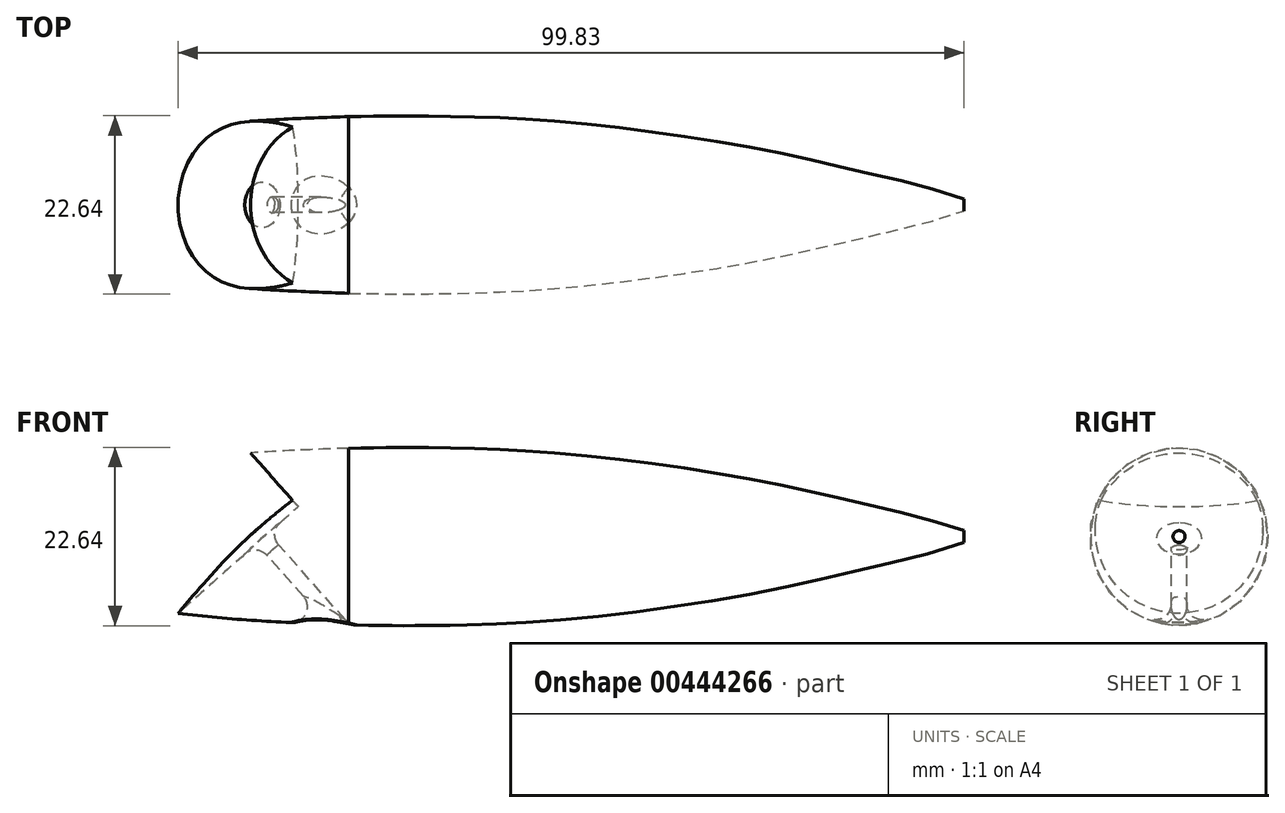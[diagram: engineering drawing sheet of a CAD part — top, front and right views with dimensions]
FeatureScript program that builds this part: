
annotation { "Feature Type Name" : "Feature", "Feature Type Description" : "" }
export const myFeature = defineFeature(function(context is Context, id is Id, definition is map)
    precondition{}
    {
        {
            var Q0;
            Q0=qCreatedBy(makeId("Top.planeOp"),FACE);
            var sketch = newSketch(context, id + "F0", { "sketchPlane" : qUnion([Q0])});
            skFitSpline(sketch, "E0", {"points": [v(50.74, 0.76) * mm, v(40.36, 3.6) * mm, v(27.98, 6.45) * mm, v(13.03, 9.02) * mm, v(-1.08, 10.63) * mm, v(-11.73, 11.19) * mm, v(-22.12, 11.3) * mm, v(-27.42, 11.23) * mm], "startDerivative": vector(-105.08, 35.47) * mm, "endDerivative": vector(-52.2, -0.15) * mm});
            skLineSegment(sketch, "E1", {"start": v(0, 0) * mm, "end": v(-76.2, 0) * mm});
            skFitSpline(sketch, "E2.MirrorCS", {"points": [v(50.74, -0.76) * mm, v(40.36, -3.6) * mm, v(27.98, -6.45) * mm, v(13.03, -9.02) * mm, v(-1.08, -10.63) * mm, v(-11.73, -11.19) * mm, v(-22.12, -11.3) * mm, v(-27.42, -11.23) * mm], "startDerivative": vector(-105.08, -35.47) * mm, "endDerivative": vector(-52.2, 0.15) * mm});
            skLineSegment(sketch, "E3", {"start": v(50.74, 0.76) * mm, "end": v(50.74, -0.76) * mm});
            skLineSegment(sketch, "E4", {"start": v(-27.42, 11.23) * mm, "end": v(-27.42, -11.23) * mm});
            skFitSpline(sketch, "E5", {"points": [v(-27.42, -11.23) * mm, v(-50.83, -9.56) * mm], "startDerivative": vector(-27.1, 0.96) * mm, "endDerivative": vector(-25.61, 3.15) * mm});
            skLineSegment(sketch, "E6", {"start": v(-27.42, 0) * mm, "end": v(50.74, 0) * mm});
            skFitSpline(sketch, "E7.MirrorCS", {"points": [v(-27.42, 11.23) * mm, v(-50.83, 9.56) * mm], "startDerivative": vector(-27.1, -0.96) * mm, "endDerivative": vector(-25.61, -3.15) * mm});
            skLineSegment(sketch, "E8", {"start": v(-50.83, -9.56) * mm, "end": v(-50.83, 9.56) * mm});
            skSolve(sketch);
        }
        {
            var Q0;
            {var subQ5=sQuery(id+"F0.wireOp",EDGE,"E0");Q0=makeQuery(id+"F0.imprint","IMPRINT",FACE,{"disambiguationData":[TD([[makeQuery(id+"F0.imprint","IMPRINT",EDGE,{"derivedFrom":subQ5}),1.0]])]});}
            var Q1;
            {var subQ5=sQuery(id+"F0.wireOp",EDGE,"E7.MirrorCS");Q1=makeQuery(id+"F0.imprint","IMPRINT",FACE,{"disambiguationData":[TD([[makeQuery(id+"F0.imprint","IMPRINT",EDGE,{"derivedFrom":subQ5}),1.0]])]});}
            var Q2;
            Q2=sQuery(id+"F0.wireOp",EDGE,"E1");
            revolve(context, id + "F1", {"entities" : qUnion([Q0, Q1]), "axis" : qUnion([Q2]), "revolveType" : RevolveType.FULL});
        }
        {
            var Q0;
            Q0=qCreatedBy(makeId("Front.planeOp"),FACE);
            var sketch = newSketch(context, id + "F2", { "sketchPlane" : qUnion([Q0])});
            skLineSegment(sketch, "E9.0", {"start": v(-50.83, 9.56) * mm, "end": v(-50.83, -9.56) * mm});
            skLineSegment(sketch, "E10", {"start": v(-50.83, -9.56) * mm, "end": v(-34.7, 4.79) * mm});
            skLineSegment(sketch, "E11", {"start": v(-34.7, 4.79) * mm, "end": v(-39.93, 10.67) * mm});
            skFitSpline(sketch, "E12", {"points": [v(-39.93, 10.67) * mm, v(-50.83, 9.56) * mm], "startDerivative": vector(-10.94, -0.63) * mm, "endDerivative": vector(-11.09, -1.8) * mm});
            skSolve(sketch);
        }
        {
            var Q0;
            Q0=makeQuery(id+"F2.imprint","IMPRINT",FACE,{"disambiguationData":[TD([[makeQuery(id+"F2.imprint","IMPRINT",EDGE,{"derivedFrom":sQuery(id+"F2.wireOp",EDGE,"E9.0")}),1.0]])]});
            extrude(context, id + "F3", {"entities" : qUnion([Q0]), "operationType" : NewBodyOperationType.REMOVE, "endBound" : BoundingType.SYMMETRIC, "oppositeDirection" : true, "depth" : 25.4 * mm});
        }
        {
            var Q0;
            Q0=makeQuery(id+"F3.boolean.opBoolean","COPY",FACE,{"derivedFrom":makeQuery(id+"F3.opExtrude","SWEPT_FACE",FACE,{"disambiguationData":[OSD([sQuery(id+"F2.wireOp",EDGE,"E11")])]})});
            var sketch = newSketch(context, id + "F4", { "sketchPlane" : qUnion([Q0])});
            skFitSpline(sketch, "E13", {"points": [v(10.62, 26.64) * mm, v(-10.64, 26.64) * mm], "startDerivative": vector(-14.87, -5.24) * mm, "endDerivative": vector(-14.04, 5.24) * mm});
            skLineSegment(sketch, "E14", {"start": v(-10.64, 26.64) * mm, "end": v(10.62, 26.64) * mm});
            skSolve(sketch);
        }
        {
            var Q0;
            {var subQ0=sQuery(id+"F4.wireOp",EDGE,"E13");Q0=makeQuery(id+"F4.imprint","IMPRINT",FACE,{"disambiguationData":[TD([[makeQuery(id+"F4.imprint","IMPRINT",EDGE,{"derivedFrom":subQ0}),-1.0]])]});}
            extrude(context, id + "F5", {"entities" : qUnion([Q0]), "operationType" : NewBodyOperationType.REMOVE, "endBound" : BoundingType.THROUGH_ALL, "depth" : 25.4 * mm});
        }
        {
            var Q0;
            Q0=makeQuery(id+"F3.boolean.opBoolean","COPY",FACE,{"derivedFrom":makeQuery(id+"F3.opExtrude","SWEPT_FACE",FACE,{"disambiguationData":[OSD([sQuery(id+"F2.wireOp",EDGE,"E10")])]})});
            var sketch = newSketch(context, id + "F6", { "sketchPlane" : qUnion([Q0])});
            skLineSegment(sketch, "E15", {"start": v(-21.97, 0) * mm, "end": v(-28.83, 0) * mm, "construction": true});
            skCircle(sketch, "E16", {"center": v(-28.83, 0) * mm, "radius": 1 * mm});
            skSolve(sketch);
        }
        {
            var Q0;
            Q0=makeQuery(id+"F6.imprint","IMPRINT",FACE,{"disambiguationData":[TD([[makeQuery(id+"F6.imprint","IMPRINT",EDGE,{"derivedFrom":sQuery(id+"F6.wireOp",EDGE,"E16")}),1.0]])]});
            extrude(context, id + "F7", {"entities" : qUnion([Q0]), "operationType" : NewBodyOperationType.REMOVE, "oppositeDirection" : true, "depth" : 25.4 * mm});
        }
        {
            var Q0;
            Q0=makeQuery(id+"F7.boolean.opBoolean","INTERSECT",EDGE,{"derivedFrom":[makeQuery(id+"F5.boolean.opBoolean","COPY",FACE,{"derivedFrom":makeQuery(id+"F5.opExtrude","SWEPT_FACE",FACE,{"disambiguationData":[OSD([sQuery(id+"F4.wireOp",EDGE,"E13")])]})}),makeQuery(id+"F7.opExtrude","SWEPT_FACE",FACE,{"disambiguationData":[OSD([sQuery(id+"F6.wireOp",EDGE,"E16")])]})]});
            fillet(context, id + "F8", {"entities" : qUnion([Q0]), "radius" : 2 * mm, "tangentPropagation" : true, "allowEdgeOverflow" : false});
        }
        {
            var Q0;
            Q0=makeQuery(id+"F7.boolean.opBoolean","INTERSECT",EDGE,{"derivedFrom":[makeQuery(id+"F1.opRevolve","SWEPT_FACE",FACE,{"disambiguationData":[OSD([sQuery(id+"F0.wireOp",EDGE,"E7.MirrorCS")])]}),makeQuery(id+"F7.opExtrude","SWEPT_FACE",FACE,{"disambiguationData":[OSD([sQuery(id+"F6.wireOp",EDGE,"E16")])]})]});
            var Q1;
            Q1=makeQuery(id+"F7.boolean.opBoolean","INTERSECT",EDGE,{"derivedFrom":[makeQuery(id+"F1.opRevolve","SWEPT_FACE",FACE,{"disambiguationData":[OSD([sQuery(id+"F0.wireOp",EDGE,"E0")])]}),makeQuery(id+"F7.opExtrude","SWEPT_FACE",FACE,{"disambiguationData":[OSD([sQuery(id+"F6.wireOp",EDGE,"E16")])]})]});
            fillet(context, id + "F9", {"entities" : qUnion([Q0, Q1]), "radius" : 2 * mm, "tangentPropagation" : true, "allowEdgeOverflow" : false});
        }
        {
            var Q0;
            Q0=qCreatedBy(makeId("Front.planeOp"),FACE);
            var sketch = newSketch(context, id + "F10", { "sketchPlane" : qUnion([Q0])});
            skFitSpline(sketch, "E17.0", {"points": [v(-34.7, 4.79) * mm, v(-34.12, 4.14) * mm, v(-33.83, 3.82) * mm, v(-33.83, 3.81) * mm]});
            skPoint(sketch, "E18", {"position": v(-34.55, 4.62) * mm});
            skLineSegment(sketch, "E19", {"start": v(-34.55, 4.62) * mm, "end": v(50.9, 0) * mm});
            skLineSegment(sketch, "E20", {"start": v(-24.57, 16.63) * mm, "end": v(-45.81, 12.1) * mm});
            skLineSegment(sketch, "E21", {"start": v(-45.81, 12.1) * mm, "end": v(-34.55, 4.62) * mm});
            skLineSegment(sketch, "E22", {"start": v(50.9, 0) * mm, "end": v(55.75, 11.19) * mm});
            skLineSegment(sketch, "E23", {"start": v(55.75, 11.19) * mm, "end": v(-24.57, 16.63) * mm});
            skLineSegment(sketch, "E24", {"start": v(50.9, 0) * mm, "end": v(57.12, -13.7) * mm});
            skLineSegment(sketch, "E25", {"start": v(57.12, -13.7) * mm, "end": v(-52.13, -12.87) * mm});
            skLineSegment(sketch, "E26", {"start": v(-52.13, -12.87) * mm, "end": v(-52.86, -5.28) * mm});
            skLineSegment(sketch, "E27", {"start": v(-52.86, -5.28) * mm, "end": v(-34.7, 4.79) * mm});
            skSolve(sketch);
        }
        {
            var Q0;
            Q0=makeQuery(id+"F1.opRevolve","SWEPT_BODY",BODY,{"disambiguationData":[OSD([sQuery(id+"F0.wireOp",EDGE,"E0"),sQuery(id+"F0.wireOp",EDGE,"E1"),sQuery(id+"F0.wireOp",EDGE,"E3"),sQuery(id+"F0.wireOp",EDGE,"E6"),sQuery(id+"F0.wireOp",EDGE,"E7.MirrorCS"),sQuery(id+"F0.wireOp",EDGE,"E8")])]});
            transform(context, id + "F11", {"entities" : qUnion([Q0]), "transformType" : TransformType.TRANSLATION_3D, "dx" : 0 * mm, "dy" : 0 * mm, "dz" : 0 * mm, "makeCopy" : true});
        }
    });
